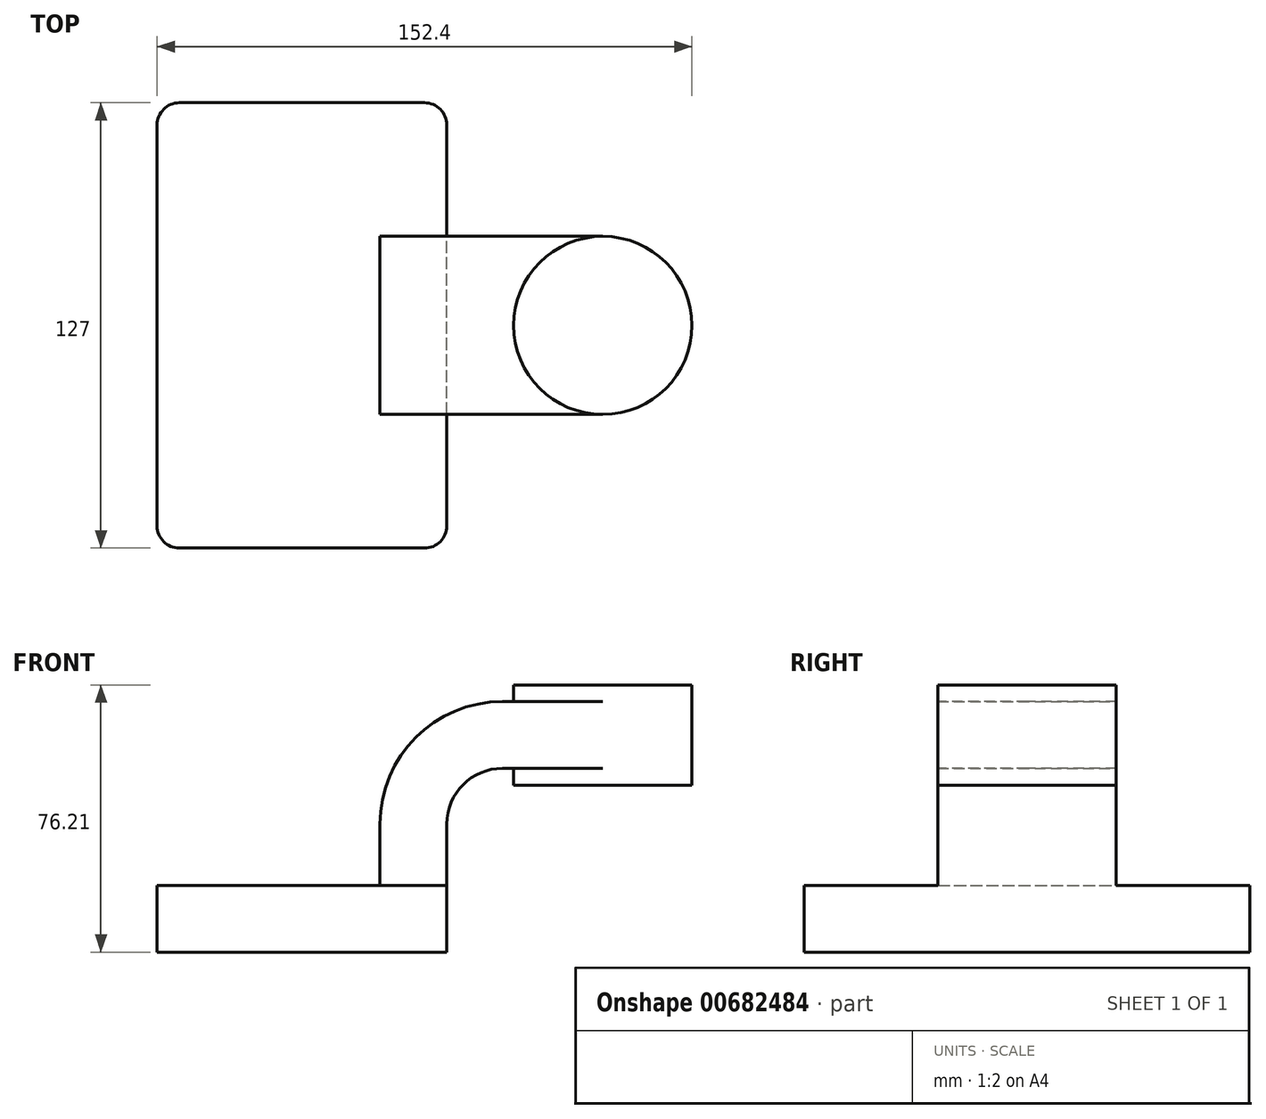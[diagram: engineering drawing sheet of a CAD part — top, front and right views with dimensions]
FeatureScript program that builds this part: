
annotation { "Feature Type Name" : "Feature", "Feature Type Description" : "" }
export const myFeature = defineFeature(function(context is Context, id is Id, definition is map)
    precondition{}
    {
        {
            var Q0;
            Q0=qCreatedBy(makeId("Front.planeOp"),FACE);
            var sketch = newSketch(context, id + "F0", { "sketchPlane" : qUnion([Q0])});
            skLineSegment(sketch, "E0.bottom", {"start": v(41.27, 9.53) * mm, "end": v(-41.28, 9.53) * mm});
            skLineSegment(sketch, "E0.top", {"start": v(41.28, -9.52) * mm, "end": v(-41.27, -9.52) * mm});
            skLineSegment(sketch, "E0.left", {"start": v(41.28, 9.53) * mm, "end": v(41.28, -9.52) * mm});
            skLineSegment(sketch, "E0.right", {"start": v(-41.28, 9.53) * mm, "end": v(-41.27, -9.52) * mm});
            skPoint(sketch, "E0.middle", {"position": v(0, 0) * mm});
            skLineSegment(sketch, "E1", {"start": v(41.27, 9.53) * mm, "end": v(41.27, 27) * mm});
            skLineSegment(sketch, "E2.bottom", {"start": v(60.33, 38.1) * mm, "end": v(111.13, 38.1) * mm});
            skLineSegment(sketch, "E2.top", {"start": v(60.32, 66.68) * mm, "end": v(111.12, 66.68) * mm});
            skLineSegment(sketch, "E2.left", {"start": v(60.33, 38.1) * mm, "end": v(60.32, 66.68) * mm});
            skLineSegment(sketch, "E2.right", {"start": v(111.13, 38.1) * mm, "end": v(111.12, 66.68) * mm});
            skPoint(sketch, "E2.middle", {"position": v(85.73, 52.39) * mm});
            skArc(sketch, "E3", {"start": v(41.27, 27) * mm, "mid": v(45.92, 38.23) * mm, "end": v(57.15, 42.88) * mm});
            skLineSegment(sketch, "E4", {"start": v(57.15, 42.88) * mm, "end": v(85.72, 42.88) * mm});
            skLineSegment(sketch, "E5.0", {"start": v(57.15, 61.93) * mm, "end": v(85.72, 61.93) * mm});
            skArc(sketch, "E5.1", {"start": v(22.23, 27) * mm, "mid": v(32.45, 51.7) * mm, "end": v(57.15, 61.93) * mm});
            skLineSegment(sketch, "E5.2", {"start": v(22.22, 9.53) * mm, "end": v(22.22, 27) * mm});
            skLineSegment(sketch, "E6", {"start": v(85.72, 38.1) * mm, "end": v(85.72, 66.68) * mm});
            skFitSpline(sketch, "E7", {"points": [v(-41.28, 9.53) * mm, v(57.15, 61.93) * mm], "startDerivative": vector(1.4, 79.9) * mm, "endDerivative": vector(114.47, -1.08) * mm});
            skSolve(sketch);
        }
        {
            var Q0;
            Q0=makeQuery(id+"F0.imprint","IMPRINT",FACE,{"disambiguationData":[TD([[makeQuery(id+"F0.imprint","IMPRINT",EDGE,{"derivedFrom":sQuery(id+"F0.wireOp",EDGE,"E0.top")}),-1.0]])]});
            extrude(context, id + "F1", {"entities" : qUnion([Q0]), "endBound" : BoundingType.SYMMETRIC, "depth" : 127 * mm, "offsetDistance" : 25.4 * mm});
        }
        {
            var Q0;
            {var subQ6=sQuery(id+"F0.wireOp",EDGE,"E1");Q0=makeQuery(id+"F0.imprint","IMPRINT",FACE,{"disambiguationData":[TD([[makeQuery(id+"F0.imprint","IMPRINT",EDGE,{"derivedFrom":subQ6}),1.0]])]});}
            var Q1;
            {var subQ0=sQuery(id+"F0.wireOp",EDGE,"E4");var subQ1=sQuery(id+"F0.wireOp",EDGE,"E2.left");var subQ2=makeQuery(id+"F0.imprint","INTERSECT",VERTEX,{"derivedFrom":[subQ1,subQ0]});Q1=makeQuery(id+"F0.imprint","IMPRINT",FACE,{"disambiguationData":[TD([[makeQuery(id+"F0.imprint","IMPRINT",EDGE,{"disambiguationData":[TD([[subQ2,-1.0]])],"derivedFrom":subQ1}),-1.0]])]});}
            extrude(context, id + "F2", {"entities" : qUnion([Q0, Q1]), "operationType" : NewBodyOperationType.ADD, "endBound" : BoundingType.SYMMETRIC, "depth" : 50.8 * mm, "offsetDistance" : 25.4 * mm});
        }
        {
            var Q0;
            Q0=makeQuery(id+"F0.imprint","IMPRINT",FACE,{"disambiguationData":[TD([[makeQuery(id+"F0.imprint","IMPRINT",EDGE,{"derivedFrom":sQuery(id+"F0.wireOp",EDGE,"E5.1")}),1.0]])]});
            extrude(context, id + "F3", {"entities" : qUnion([Q0]), "operationType" : NewBodyOperationType.ADD, "endBound" : BoundingType.SYMMETRIC, "depth" : 15.88 * mm, "offsetDistance" : 25.4 * mm});
        }
        {
            var Q0;
            {var subQ4=sQuery(id+"F0.wireOp",EDGE,"E2.right");Q0=makeQuery(id+"F0.imprint","IMPRINT",FACE,{"disambiguationData":[TD([[makeQuery(id+"F0.imprint","IMPRINT",EDGE,{"derivedFrom":subQ4}),1.0]])]});}
            var Q1;
            Q1=sQuery(id+"F0.wireOp",EDGE,"E6");
            revolve(context, id + "F4", {"operationType" : NewBodyOperationType.ADD, "entities" : qUnion([Q0]), "axis" : qUnion([Q1]), "revolveType" : RevolveType.FULL});
        }
        {
            var Q0;
            Q0=makeQuery(id+"F1.opExtrude","CAP_EDGE",EDGE,{"disambiguationData":[OSD([sQuery(id+"F0.wireOp",EDGE,"E0.left")])],"isStart":false});
            var Q1;
            Q1=makeQuery(id+"F1.opExtrude","CAP_EDGE",EDGE,{"disambiguationData":[OSD([sQuery(id+"F0.wireOp",EDGE,"E0.left")])],"isStart":true});
            var Q2;
            Q2=makeQuery(id+"F1.opExtrude","CAP_EDGE",EDGE,{"disambiguationData":[OSD([sQuery(id+"F0.wireOp",EDGE,"E0.right")])],"isStart":true});
            var Q3;
            Q3=makeQuery(id+"F1.opExtrude","CAP_EDGE",EDGE,{"disambiguationData":[OSD([sQuery(id+"F0.wireOp",EDGE,"E0.right")])],"isStart":false});
            fillet(context, id + "F5", {"entities" : qUnion([Q0, Q1, Q2, Q3]), "radius" : 6.35 * mm, "tangentPropagation" : true, "allowEdgeOverflow" : false});
        }
    });
